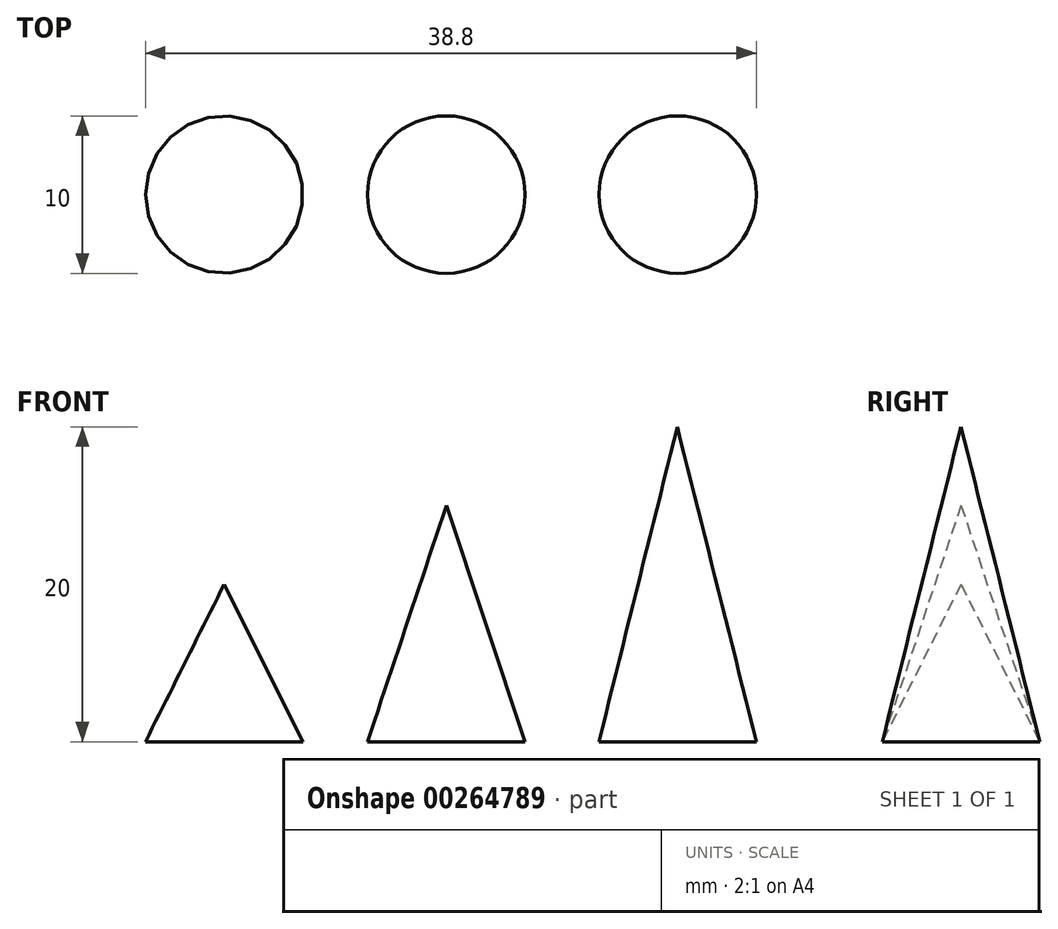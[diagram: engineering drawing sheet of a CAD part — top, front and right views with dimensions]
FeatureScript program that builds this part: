
annotation { "Feature Type Name" : "Feature", "Feature Type Description" : "" }
export const myFeature = defineFeature(function(context is Context, id is Id, definition is map)
    precondition{}
    {
        {
            var Q0;
            Q0=qCreatedBy(makeId("Top.planeOp"),FACE);
            var sketch = newSketch(context, id + "F0", { "sketchPlane" : qUnion([Q0])});
            skCircle(sketch, "E0", {"center": v(0, 0) * mm, "radius": 5 * mm});
            skLineSegment(sketch, "E1", {"start": v(-5, 0) * mm, "end": v(5, 0) * mm, "construction": true});
            skCircle(sketch, "E2", {"center": v(14.7, 0) * mm, "radius": 5 * mm});
            skLineSegment(sketch, "E3", {"start": v(9.7, 0) * mm, "end": v(19.7, 0) * mm, "construction": true});
            skCircle(sketch, "E4", {"center": v(-14.1, 0) * mm, "radius": 5 * mm});
            skLineSegment(sketch, "E5", {"start": v(-19.1, 0) * mm, "end": v(-9.1, 0) * mm, "construction": true});
            skSolve(sketch);
        }
        {
            var Q0;
            Q0=qCreatedBy(makeId("Top.planeOp"),FACE);
            cPlane(context, id + "F1", {"entities" : qUnion([Q0]), "cplaneType" : CPlaneType.OFFSET, "offset" : 15 * mm, "width" : 150 * mm, "height" : 150 * mm});
        }
        {
            var Q0;
            Q0=qCreatedBy(id+"F1.planeOp",FACE);
            var sketch = newSketch(context, id + "F2", { "sketchPlane" : qUnion([Q0])});
            skPoint(sketch, "E6", {"position": v(0, 0) * mm});
            skSolve(sketch);
        }
        {
            var Q0;
            Q0=makeQuery(id+"F0.imprint","IMPRINT",FACE,{"disambiguationData":[TD([[makeQuery(id+"F0.imprint","IMPRINT",EDGE,{"derivedFrom":sQuery(id+"F0.wireOp",EDGE,"E0")}),1.0]])]});
            var Q1;
            Q1=sQuery(id+"F2.wireOp",VERTEX,"E6");
            loft(context, id + "F3", {"sheetProfilesArray" : [{ "sheetProfileEntities" : qUnion([Q0]) }, { "sheetProfileEntities" : qUnion([Q1]) }]});
        }
        {
            var Q0;
            Q0=qCreatedBy(makeId("Top.planeOp"),FACE);
            cPlane(context, id + "F4", {"entities" : qUnion([Q0]), "cplaneType" : CPlaneType.OFFSET, "offset" : 20 * mm, "width" : 150 * mm, "height" : 150 * mm});
        }
        {
            var Q0;
            Q0=qCreatedBy(id+"F4.planeOp",FACE);
            var sketch = newSketch(context, id + "F5", { "sketchPlane" : qUnion([Q0])});
            skPoint(sketch, "E7", {"position": v(14.67, 0) * mm});
            skSolve(sketch);
        }
        {
            var Q0;
            Q0=makeQuery(id+"F0.imprint","IMPRINT",FACE,{"disambiguationData":[TD([[makeQuery(id+"F0.imprint","IMPRINT",EDGE,{"derivedFrom":sQuery(id+"F0.wireOp",EDGE,"E2")}),1.0]])]});
            var Q1;
            Q1=sQuery(id+"F5.wireOp",VERTEX,"E7");
            loft(context, id + "F6", {"sheetProfilesArray" : [{ "sheetProfileEntities" : qUnion([Q0]) }, { "sheetProfileEntities" : qUnion([Q1]) }]});
        }
        {
            var Q0;
            Q0=qCreatedBy(makeId("Top.planeOp"),FACE);
            cPlane(context, id + "F7", {"entities" : qUnion([Q0]), "cplaneType" : CPlaneType.OFFSET, "offset" : 10 * mm, "width" : 150 * mm, "height" : 150 * mm});
        }
        {
            var Q0;
            Q0=qCreatedBy(id+"F7.planeOp",FACE);
            var sketch = newSketch(context, id + "F8", { "sketchPlane" : qUnion([Q0])});
            skPoint(sketch, "E8", {"position": v(-14.1, 0) * mm});
            skSolve(sketch);
        }
        {
            var Q0;
            Q0=makeQuery(id+"F0.imprint","IMPRINT",FACE,{"disambiguationData":[TD([[makeQuery(id+"F0.imprint","IMPRINT",EDGE,{"derivedFrom":sQuery(id+"F0.wireOp",EDGE,"E4")}),1.0]])]});
            var Q1;
            Q1=sQuery(id+"F8.wireOp",VERTEX,"E8");
            loft(context, id + "F9", {"sheetProfilesArray" : [{ "sheetProfileEntities" : qUnion([Q0]) }, { "sheetProfileEntities" : qUnion([Q1]) }]});
        }
    });
